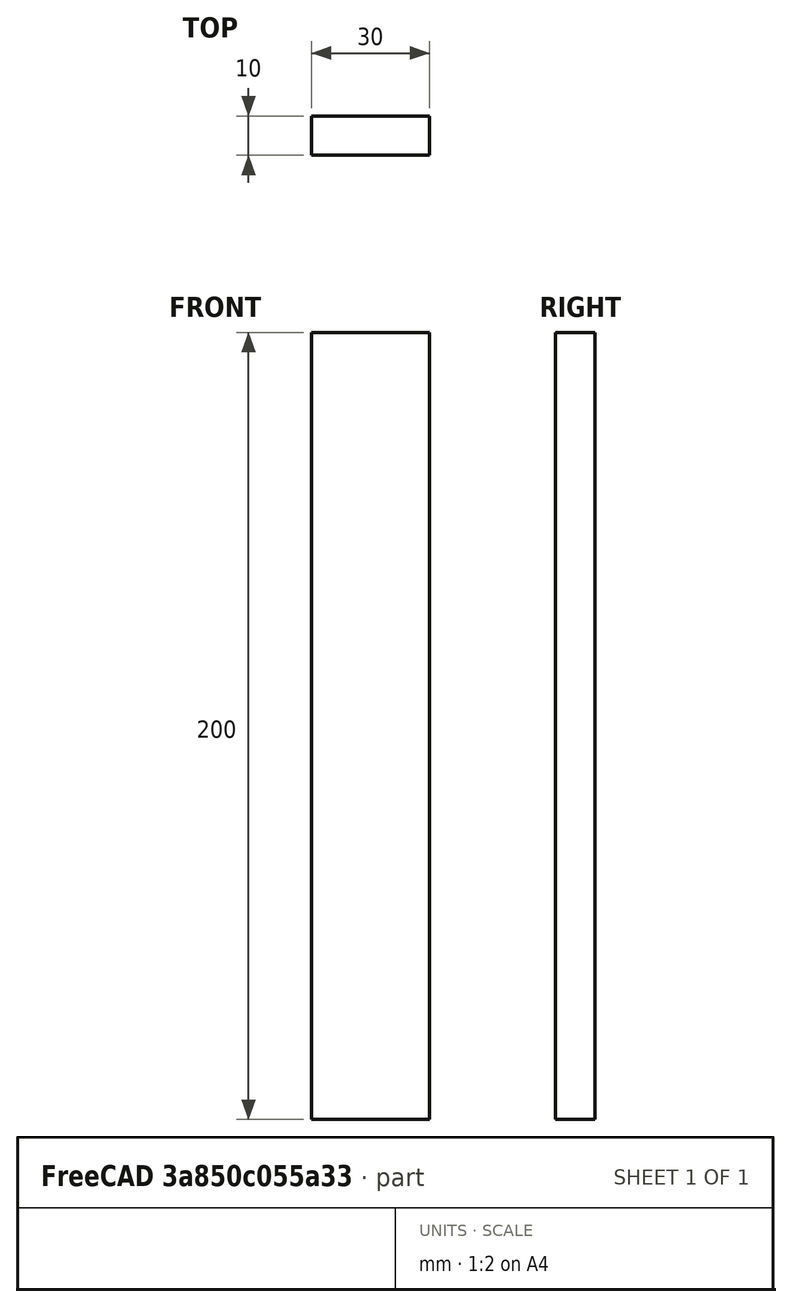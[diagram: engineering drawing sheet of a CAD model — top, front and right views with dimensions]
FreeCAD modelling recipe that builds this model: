
FCSTD DOCUMENT  (FreeCAD 0.21R33771 (Git))
Label: reflector_2024_listello_handle
License: All rights reserved
LicenseURL: https://en.wikipedia.org/wiki/All_rights_reserved
objects: Sketcher::SketchObject×1, PartDesign::Pad×1, PartDesign::Body×1
note: 4 computed .brp shape members not serialized (recipe doc carries the construction recipe); baked Part::Feature solids carry a one-line shape summary decoded from their .brp

FEATURE [Sketcher::SketchObject] Sketch
  FullyConstrained = true
  MapMode = 5
  Placement = pos=(0,0,0) rot=(1,0,0;1.5708rad)
  Support = -> [XZ_Plane]
  sketch-geometry (4):
    g0: LineSegment StartX=-15 StartY=100 StartZ=0 EndX=15 EndY=100 EndZ=0
    g1: LineSegment StartX=15 StartY=100 StartZ=0 EndX=15 EndY=-100 EndZ=0
    g2: LineSegment StartX=15 StartY=-100 StartZ=0 EndX=-15 EndY=-100 EndZ=0
    g3: LineSegment StartX=-15 StartY=-100 StartZ=0 EndX=-15 EndY=100 EndZ=0
  constraints (10):
    c: Coincident(g0,g1)
    c: Coincident(g1,g2)
    c: Coincident(g2,g3)
    c: Coincident(g3,g0)
    c: Horizontal(g2)
    c: Vertical(g3)
    c: Symmetric(g0,g0,g-2)
    c: Symmetric(g1,g0,g-1)
    c: DistanceX(g0,g0) = 30
    c: DistanceY(g1,g1) = 200
FEATURE [PartDesign::Pad] Pad
  Direction = (0,-1,-2e-16)
  Length = 10
  Length2 = 10
  Placement = pos=(0,0,0) rot=(1,0,0;1.5708rad)
  Profile = -> Sketch
  ReferenceAxis = -> Sketch [N_Axis]
  Type = 0
FEATURE [PartDesign::Body] Body  label="listello_handle"
  Group = -> [Sketch,Pad]
  Origin = -> Origin
  Tip = -> Pad
